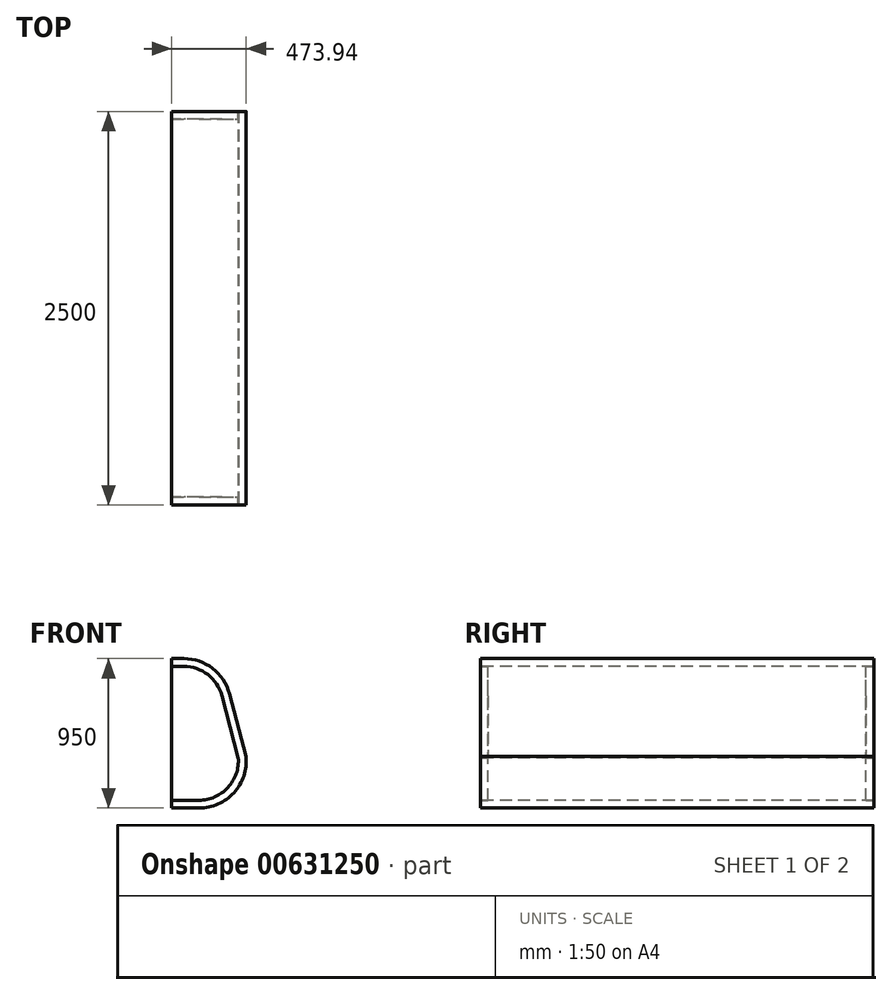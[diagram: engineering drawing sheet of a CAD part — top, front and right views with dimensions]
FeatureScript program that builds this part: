
annotation { "Feature Type Name" : "Feature", "Feature Type Description" : "" }
export const myFeature = defineFeature(function(context is Context, id is Id, definition is map)
    precondition{}
    {
        {
            var Q0;
            Q0=qCreatedBy(makeId("Front.planeOp"),FACE);
            var sketch = newSketch(context, id + "F0", { "sketchPlane" : qUnion([Q0])});
            skLineSegment(sketch, "E0", {"start": v(847.8, -584.8) * mm, "end": v(847.8, 265.2) * mm});
            skLineSegment(sketch, "E1", {"start": v(847.8, 265.2) * mm, "end": v(925.22, 265.2) * mm});
            skLineSegment(sketch, "E2", {"start": v(1166.94, 79) * mm, "end": v(1270.93, -314.93) * mm});
            skLineSegment(sketch, "E3", {"start": v(1021.73, -584.8) * mm, "end": v(847.8, -584.8) * mm});
            skPoint(sketch, "E4.visualSharp", {"position": v(1117.8, 265.2) * mm});
            skArc(sketch, "E4.filletArc", {"start": v(1166.94, 79) * mm, "mid": v(1077.78, 213.25) * mm, "end": v(925.22, 265.2) * mm});
            skArc(sketch, "E5.filletArc", {"start": v(1021.73, -584.8) * mm, "mid": v(1205.4, -504.41) * mm, "end": v(1270.93, -314.93) * mm});
            skSolve(sketch);
        }
        {
            var Q0;
            Q0=makeQuery(id+"F0.imprint","IMPRINT",FACE,{"disambiguationData":[TD([[makeQuery(id+"F0.imprint","IMPRINT",EDGE,{"derivedFrom":sQuery(id+"F0.wireOp",EDGE,"E0")}),-1.0]])]});
            extrude(context, id + "F1", {"entities" : qUnion([Q0]), "depth" : 50 * mm, "offsetDistance" : 25 * mm});
        }
        {
            var Q0;
            Q0=makeQuery(id+"F1.opExtrude","CAP_FACE",FACE,{"disambiguationData":[OSD([sQuery(id+"F0.wireOp",EDGE,"E0"),sQuery(id+"F0.wireOp",EDGE,"E1"),sQuery(id+"F0.wireOp",EDGE,"E2"),sQuery(id+"F0.wireOp",EDGE,"31BhLn3U-khXQ-2pwS-5fV9-i5ZksB1RNIWn"),sQuery(id+"F0.wireOp",EDGE,"E3"),sQuery(id+"F0.wireOp",EDGE,"E4.filletArc"),sQuery(id+"F0.wireOp",EDGE,"E5.filletArc")])],"isStart":false});
            var sketch = newSketch(context, id + "F2", { "sketchPlane" : qUnion([Q0])});
            skLineSegment(sketch, "E6", {"start": v(847.8, 265.2) * mm, "end": v(925.22, 265.2) * mm});
            skArc(sketch, "E7", {"start": v(1166.94, 79) * mm, "mid": v(1077.78, 213.25) * mm, "end": v(925.22, 265.2) * mm});
            skLineSegment(sketch, "E8", {"start": v(1166.94, 79) * mm, "end": v(1166.94, 79) * mm});
            skLineSegment(sketch, "E9", {"start": v(1320.37, -306.3) * mm, "end": v(1215.29, 91.76) * mm});
            skLineSegment(sketch, "E10", {"start": v(925.22, 315.2) * mm, "end": v(847.8, 315.2) * mm});
            skLineSegment(sketch, "E11", {"start": v(847.8, 315.2) * mm, "end": v(847.8, 265.2) * mm});
            skPoint(sketch, "E12.visualSharp", {"position": v(1156.3, 315.2) * mm});
            skArc(sketch, "E12.filletArc", {"start": v(1215.29, 91.76) * mm, "mid": v(1108.3, 252.86) * mm, "end": v(925.22, 315.2) * mm});
            skLineSegment(sketch, "E13", {"start": v(1166.94, 79) * mm, "end": v(1270.93, -314.93) * mm});
            skArc(sketch, "E14", {"start": v(1021.73, -584.8) * mm, "mid": v(1205.4, -504.41) * mm, "end": v(1270.93, -314.93) * mm});
            skLineSegment(sketch, "E15", {"start": v(1021.73, -584.8) * mm, "end": v(847.8, -584.8) * mm});
            skLineSegment(sketch, "E16", {"start": v(847.8, -584.8) * mm, "end": v(847.8, -634.8) * mm});
            skLineSegment(sketch, "E17", {"start": v(847.8, -634.8) * mm, "end": v(1021.73, -634.8) * mm});
            skPoint(sketch, "E18.visualSharp", {"position": v(1342.31, -611.43) * mm});
            skArc(sketch, "E18.filletArc", {"start": v(1021.73, -634.8) * mm, "mid": v(1243.7, -536.6) * mm, "end": v(1320.37, -306.3) * mm});
            skSolve(sketch);
        }
        {
            var Q0;
            Q0=makeQuery(id+"F2.imprint","IMPRINT",FACE,{"disambiguationData":[TD([[makeQuery(id+"F2.imprint","IMPRINT",EDGE,{"derivedFrom":sQuery(id+"F2.wireOp",EDGE,"E6")}),1.0]])]});
            extrude(context, id + "F3", {"entities" : qUnion([Q0]), "oppositeDirection" : true, "depth" : 2500 * mm, "offsetDistance" : 25 * mm});
        }
        {
            var Q0;
            Q0=makeQuery(id+"F1.opExtrude","SWEPT_BODY",BODY,{"disambiguationData":[OSD([sQuery(id+"F0.wireOp",EDGE,"E0"),sQuery(id+"F0.wireOp",EDGE,"E1"),sQuery(id+"F0.wireOp",EDGE,"E2"),sQuery(id+"F0.wireOp",EDGE,"E3"),sQuery(id+"F0.wireOp",EDGE,"E4.filletArc"),sQuery(id+"F0.wireOp",EDGE,"E5.filletArc")])]});
            transform(context, id + "F4", {"entities" : qUnion([Q0]), "transformType" : TransformType.TRANSLATION_3D, "dx" : 0 * mm, "dy" : 2450 * mm, "dz" : 0 * mm, "makeCopy" : true});
        }
    });
